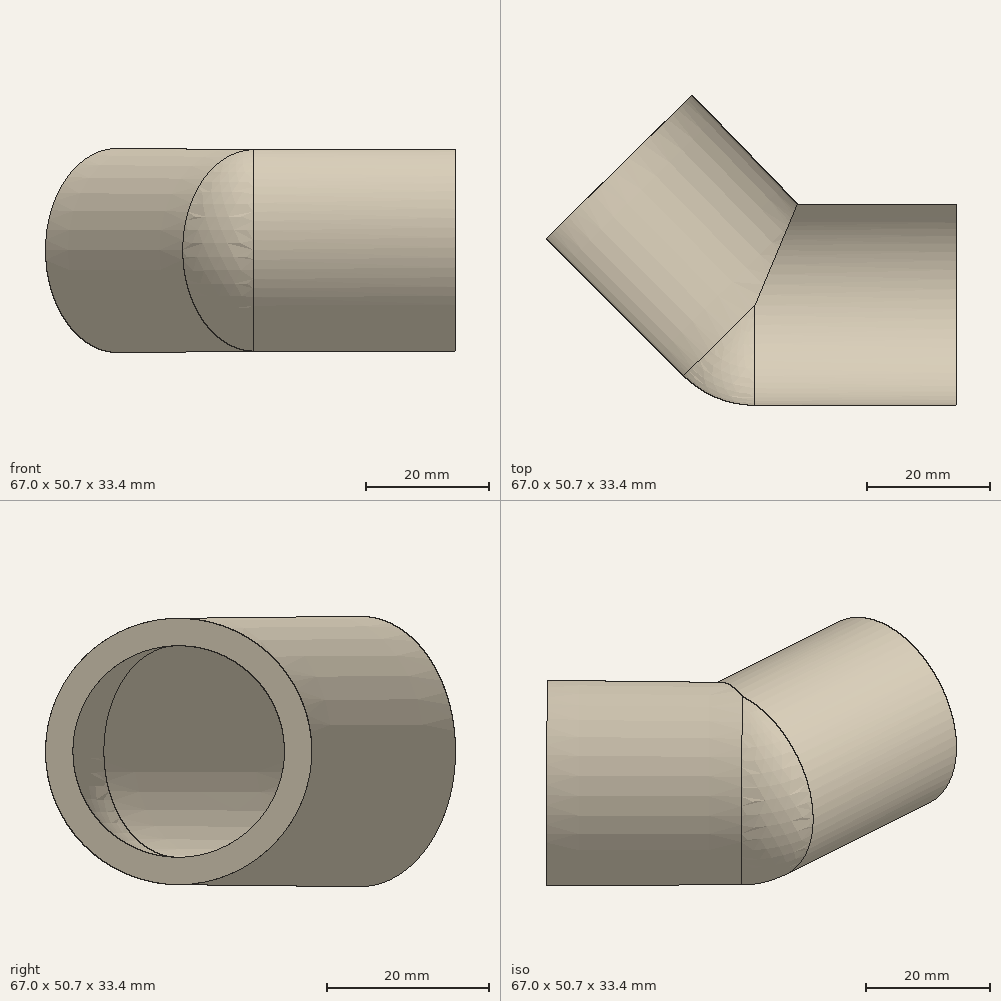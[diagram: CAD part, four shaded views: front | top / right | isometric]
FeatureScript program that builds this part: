
annotation { "Feature Type Name" : "Feature", "Feature Type Description" : "" }
export const myFeature = defineFeature(function(context is Context, id is Id, definition is map)
    precondition{}
    {
        {
            var Q0;
            Q0=qCreatedBy(makeId("Top.planeOp"),FACE);
            var sketch = newSketch(context, id + "F0", { "sketchPlane" : qUnion([Q0])});
            skLineSegment(sketch, "E0", {"start": v(32.94, 16.46) * mm, "end": v(32.94, -16.46) * mm});
            skLineSegment(sketch, "E1", {"start": v(32.94, -16.46) * mm, "end": v(20.26, -16.46) * mm});
            skLineSegment(sketch, "E2", {"start": v(32.94, -13.08) * mm, "end": v(20.26, -13.08) * mm});
            skLineSegment(sketch, "E3", {"start": v(32.94, 16.46) * mm, "end": v(7.54, 16.46) * mm});
            skLineSegment(sketch, "E4", {"start": v(32.94, 13.08) * mm, "end": v(7.54, 13.08) * mm, "construction": true});
            skLineSegment(sketch, "E5", {"start": v(-12.81, 32.03) * mm, "end": v(-31.67, 13.17) * mm});
            skLineSegment(sketch, "E6", {"start": v(-31.67, 13.17) * mm, "end": v(-9.25, -9.25) * mm});
            skLineSegment(sketch, "E7", {"start": v(-34.06, 10.78) * mm, "end": v(-11.64, -11.64) * mm});
            skLineSegment(sketch, "E8", {"start": v(-12.81, 32.03) * mm, "end": v(5.15, 14.07) * mm, "construction": true});
            skLineSegment(sketch, "E9", {"start": v(-10.42, 34.42) * mm, "end": v(7.54, 16.46) * mm});
            skLineSegment(sketch, "E10", {"start": v(20.24, 16.46) * mm, "end": v(20.24, 13.08) * mm, "construction": true});
            skLineSegment(sketch, "E11", {"start": v(26.6, -13.08) * mm, "end": v(26.6, -16.46) * mm, "construction": true});
            skLineSegment(sketch, "E12", {"start": v(-20.46, 1.96) * mm, "end": v(-22.85, -0.43) * mm, "construction": true});
            skPoint(sketch, "E12.startSnap0", {"position": v(-20.46, 1.96) * mm});
            skLineSegment(sketch, "E13", {"start": v(-3.83, 23.05) * mm, "end": v(-1.44, 25.44) * mm, "construction": true});
            skArc(sketch, "E14", {"start": v(7.54, 13.08) * mm, "mid": v(6.24, 13.34) * mm, "end": v(5.15, 14.07) * mm, "construction": true});
            skLineSegment(sketch, "E15", {"start": v(20.26, -16.46) * mm, "end": v(0, -16.46) * mm});
            skLineSegment(sketch, "E16", {"start": v(0, -13.08) * mm, "end": v(20.26, -13.08) * mm});
            skLineSegment(sketch, "E17", {"start": v(32.94, 0) * mm, "end": v(0, 0) * mm});
            skLineSegment(sketch, "E18", {"start": v(0, -13.08) * mm, "end": v(0, -16.46) * mm});
            skPoint(sketch, "E19", {"position": v(0, 0) * mm});
            skLineSegment(sketch, "E20", {"start": v(-9.25, -9.25) * mm, "end": v(-11.64, -11.64) * mm});
            skLineSegment(sketch, "E21", {"start": v(-31.67, 13.17) * mm, "end": v(-34.06, 10.78) * mm});
            skLineSegment(sketch, "E22", {"start": v(-9.25, -9.25) * mm, "end": v(0, 0) * mm});
            skLineSegment(sketch, "E23", {"start": v(0, -13.08) * mm, "end": v(0, 0) * mm});
            skLineSegment(sketch, "E24", {"start": v(0, 0) * mm, "end": v(7.54, 16.46) * mm, "construction": true});
            skLineSegment(sketch, "E25", {"start": v(-12.81, 32.03) * mm, "end": v(-10.42, 34.42) * mm});
            skLineSegment(sketch, "E26", {"start": v(-22.24, 22.6) * mm, "end": v(0, 0) * mm});
            skSolve(sketch);
        }
        {
            var Q0;
            {var subQ2=sQuery(id+"F0.wireOp",EDGE,"E1");Q0=makeQuery(id+"F0.imprint","IMPRINT",FACE,{"disambiguationData":[TD([[makeQuery(id+"F0.imprint","IMPRINT",EDGE,{"derivedFrom":subQ2}),-1.0]])]});}
            var Q1;
            Q1=sQuery(id+"F0.wireOp",EDGE,"E17");
            revolve(context, id + "F1", {"entities" : qUnion([Q0]), "axis" : qUnion([Q1]), "revolveType" : RevolveType.FULL});
        }
        {
            var Q0;
            Q0=makeQuery(id+"F0.imprint","IMPRINT",FACE,{"disambiguationData":[TD([[makeQuery(id+"F0.imprint","IMPRINT",EDGE,{"derivedFrom":sQuery(id+"F0.wireOp",EDGE,"E6")}),-1.0]])]});
            var Q1;
            Q1=sQuery(id+"F0.wireOp",EDGE,"E26");
            revolve(context, id + "F2", {"operationType" : NewBodyOperationType.ADD, "entities" : qUnion([Q0]), "axis" : qUnion([Q1]), "revolveType" : RevolveType.FULL});
        }
        {
            var Q0;
            Q0=makeQuery(id+"F1.opRevolve","SWEPT_FACE",FACE,{"disambiguationData":[OSD([sQuery(id+"F0.wireOp",EDGE,"E0")])]});
            var sketch = newSketch(context, id + "F3", { "sketchPlane" : qUnion([Q0])});
            skSolve(sketch);
        }
        {
            var Q0;
            Q0=makeQuery(id+"F3.imprint","IMPRINT",FACE,{"disambiguationData":[TD([[makeQuery(id+"F3.imprint","IMPRINT",EDGE,{"derivedFrom":makeQuery(id+"F1.opRevolve","SWEPT_EDGE",EDGE,{"disambiguationData":[OSD([sQuery(id+"F0.wireOp",EDGE,"E0"),sQuery(id+"F0.wireOp",EDGE,"E2")])]})}),1.0]])]});
            var Q1;
            Q1=sQuery(id+"F0.wireOp",VERTEX,"E19");
            extrude(context, id + "F4", {"entities" : qUnion([Q0]), "operationType" : NewBodyOperationType.REMOVE, "endBound" : BoundingType.UP_TO_VERTEX, "oppositeDirection" : true, "endBoundEntityVertex" : qUnion([Q1]), "depth" : 25.4 * mm});
        }
        {
            var Q0;
            {var subQ0=makeQuery(id+"F1.opRevolve","SWEPT_FACE",FACE,{"disambiguationData":[OSD([sQuery(id+"F0.wireOp",EDGE,"E18")])]});Q0=makeQuery(id+"F2.boolean.opBoolean","SPLIT",FACE,{"disambiguationData":[TD([makeQuery(id+"F1.opRevolve","SWEPT_FACE",FACE,{"disambiguationData":[OSD([sQuery(id+"F0.wireOp",EDGE,"E1"),sQuery(id+"F0.wireOp",EDGE,"E15")])]}),makeQuery(id+"F1.opRevolve","SWEPT_FACE",FACE,{"disambiguationData":[OSD([sQuery(id+"F0.wireOp",EDGE,"E2"),sQuery(id+"F0.wireOp",EDGE,"E16")])]}),subQ0,makeQuery(id+"F2.opRevolve","SWEPT_FACE",FACE,{"disambiguationData":[OSD([sQuery(id+"F0.wireOp",EDGE,"E6")])]}),makeQuery(id+"F2.opRevolve","SWEPT_FACE",FACE,{"disambiguationData":[OSD([sQuery(id+"F0.wireOp",EDGE,"E7")])]}),makeQuery(id+"F2.opRevolve","SWEPT_FACE",FACE,{"disambiguationData":[OSD([sQuery(id+"F0.wireOp",EDGE,"E20")])]})])],"derivedFrom":subQ0});}
            var Q1;
            Q1=makeQuery(id+"F2.boolean.opBoolean","INTERSECT",EDGE,{"disambiguationData":[OD(0.0)],"derivedFrom":[makeQuery(id+"F1.opRevolve","SWEPT_FACE",FACE,{"disambiguationData":[OSD([sQuery(id+"F0.wireOp",EDGE,"E18")])]}),makeQuery(id+"F2.opRevolve","SWEPT_FACE",FACE,{"disambiguationData":[OSD([sQuery(id+"F0.wireOp",EDGE,"E20")])]})]});
            revolve(context, id + "F5", {"operationType" : NewBodyOperationType.ADD, "entities" : qUnion([Q0]), "axis" : qUnion([Q1]), "revolveType" : RevolveType.ONE_DIRECTION, "oppositeDirection" : true, "angle" : 46 * degree});
        }
    });
